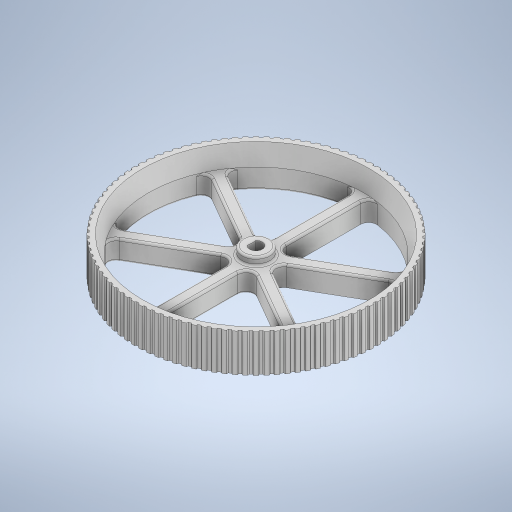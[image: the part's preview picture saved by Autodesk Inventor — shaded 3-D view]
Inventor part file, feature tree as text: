
AUTODESK INVENTOR PART (.ipt)
format: ipt  version: 2024.2 (Build 282272000, 272)  size: 1,016,320 bytes
history: native  units: mm
features: sketch x3, extrude x3, fillet x2, revolve x1
ambient origin geometry x8: Origin, YZ Plane, XZ Plane, XY Plane, X Axis, Y Axis, Z Axis, Center Point
bodies: Solid1 (feature_tree)
feature tree (9):
  revolve  "Revolution1"  [1 undecoded]
  sketch  "Sketch3"  dims[d3=30.0mm d4=360.0deg]
  extrude  "Extrusion1"  TaperAngle=360.0deg  [1 undecoded]
  extrude  "Extrusion2"  Depth=0.5mm
  extrude  "Extrusion3"  Depth=10.0mm
  fillet  "Fillet1"  Radius=7.0mm
  fillet  "Fillet2"  Radius=3.0mm
  sketch  "Sketch2"  dims[d0=3.0mm d2=5.0mm]
  sketch  "Sketch4"  dims[d5=3.2mm d6=1.15mm d7=10.0mm d8=7.0mm d9=3.0mm d10=1.5mm d11=60.0mm d13=360.0deg d15=5.0mm d16=0.0mm d17=7.0mm d18=0.0mm d19=120.0deg d20=120.0deg d21=1.6mm d22=1.0mm d23=0.5mm d24=1000.0mm d26=360.0deg d28=0.0mm d29=0.0mm d30=2.0mm d31=0.5mm d37=1.5mm d38=9.5mm d32=0.0mm d33=0.0mm d34=0.0mm d35=0.0mm]
note: 2 required parameter values undecoded (feature->parameter linkage not recoverable at this tier; creation-order binding heuristic only, values carry confidence <= 0.55)